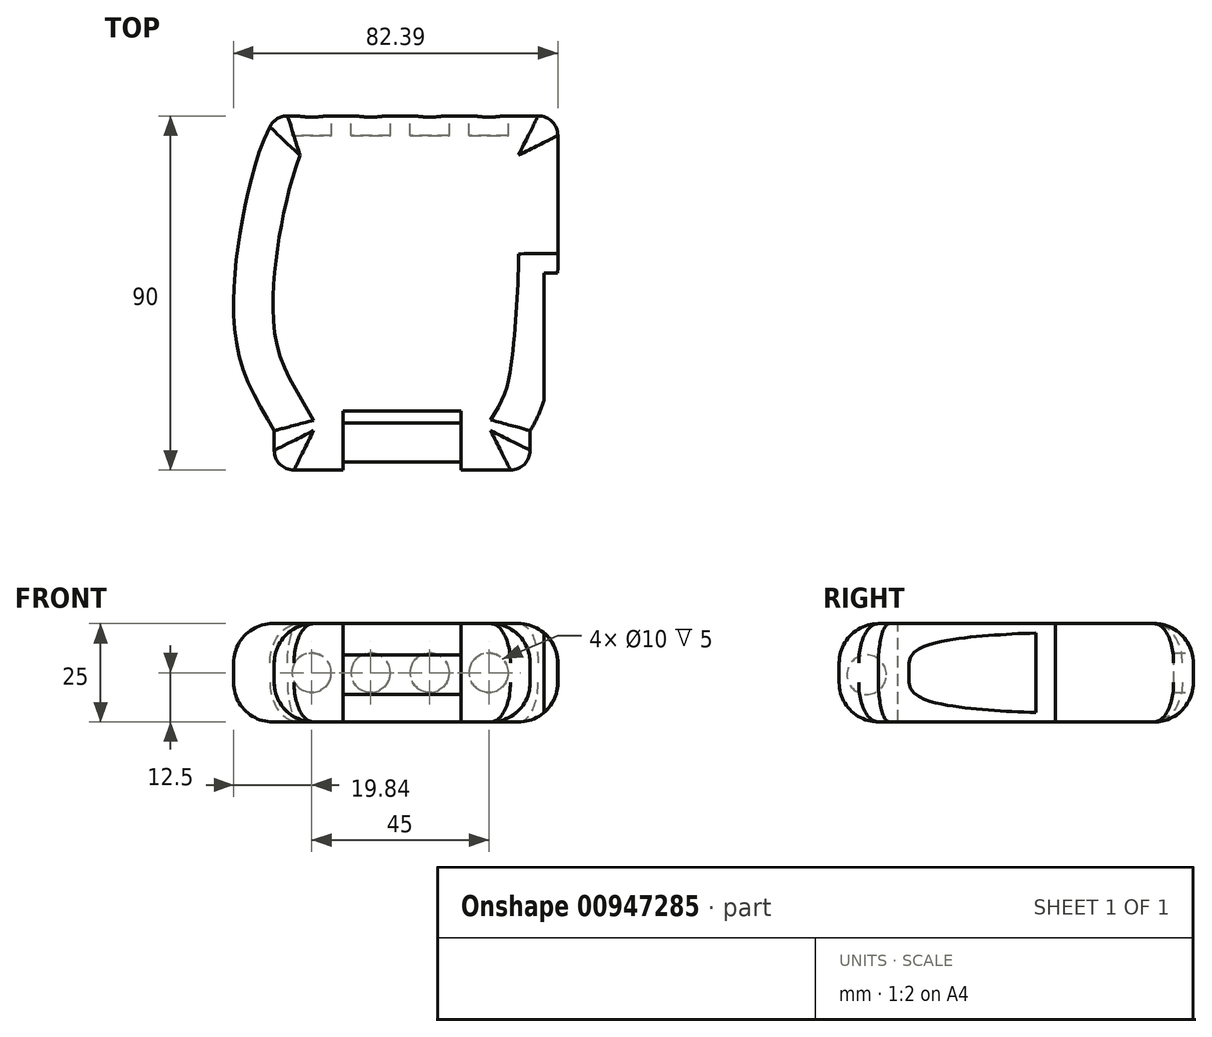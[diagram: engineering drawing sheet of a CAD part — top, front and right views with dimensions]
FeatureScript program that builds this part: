
annotation { "Feature Type Name" : "Feature", "Feature Type Description" : "" }
export const myFeature = defineFeature(function(context is Context, id is Id, definition is map)
    precondition{}
    {
        {
            var Q0;
            Q0=qCreatedBy(makeId("Top.planeOp"),FACE);
            var sketch = newSketch(context, id + "F0", { "sketchPlane" : qUnion([Q0])});
            skFitSpline(sketch, "E0", {"points": [v(-32.5, 0) * mm, v(-42.5, 25) * mm, v(-35.5, 73) * mm, v(-32.5, 80) * mm], "startDerivative": vector(-34.49, 60.35) * mm, "endDerivative": vector(0, 16.21) * mm});
            skFitSpline(sketch, "E1", {"points": [v(32.5, 0) * mm, v(37.5, 15) * mm, v(39.5, 40) * mm, v(39.5, 50) * mm], "startDerivative": vector(27.5, 45.82) * mm, "endDerivative": vector(0, 57.62) * mm});
            skLineSegment(sketch, "E2", {"start": v(-29.14, 80) * mm, "end": v(34.54, 80) * mm});
            skArc(sketch, "E3.filletArc", {"start": v(-29.14, 80) * mm, "mid": v(-31.78, 79.25) * mm, "end": v(-33.62, 77.2) * mm});
            skLineSegment(sketch, "E4", {"start": v(39.54, 75) * mm, "end": v(39.54, 45) * mm});
            skLineSegment(sketch, "E5.top", {"start": v(-27.5, -10) * mm, "end": v(27.5, -10) * mm});
            skLineSegment(sketch, "E5.left", {"start": v(-32.5, 0) * mm, "end": v(-32.5, -5) * mm});
            skLineSegment(sketch, "E5.right", {"start": v(32.5, 0) * mm, "end": v(32.5, -5) * mm});
            skArc(sketch, "E6.filletArc", {"start": v(39.54, 75) * mm, "mid": v(38.07, 78.54) * mm, "end": v(34.54, 80) * mm});
            skPoint(sketch, "E7.visualSharp", {"position": v(-32.5, -10) * mm});
            skArc(sketch, "E7.filletArc", {"start": v(-32.5, -5) * mm, "mid": v(-31.04, -8.54) * mm, "end": v(-27.5, -10) * mm});
            skPoint(sketch, "E8.visualSharp", {"position": v(32.5, -10) * mm});
            skArc(sketch, "E8.filletArc", {"start": v(27.5, -10) * mm, "mid": v(31.04, -8.54) * mm, "end": v(32.5, -5) * mm});
            skSolve(sketch);
        }
        {
            var Q0;
            Q0=makeQuery(id+"F0.imprint","IMPRINT",FACE,{"disambiguationData":[TD([[makeQuery(id+"F0.imprint","IMPRINT",EDGE,{"derivedFrom":sQuery(id+"F0.wireOp",EDGE,"E0")}),-1.0]])]});
            extrude(context, id + "F1", {"entities" : qUnion([Q0]), "depth" : 25 * mm, "offsetDistance" : 25 * mm});
        }
        {
            var Q0;
            Q0=makeQuery(id+"F1.opExtrude","CAP_FACE",FACE,{"disambiguationData":[OSD([sQuery(id+"F0.wireOp",EDGE,"49EKysyl-F1B6-WjAB-Oqjf-hUaWDvc0Rh3T"),sQuery(id+"F0.wireOp",EDGE,"E0"),sQuery(id+"F0.wireOp",EDGE,"E1"),sQuery(id+"F0.wireOp",EDGE,"E2"),sQuery(id+"F0.wireOp",EDGE,"E3.filletArc"),sQuery(id+"F0.wireOp",EDGE,"E4"),sQuery(id+"F0.wireOp",EDGE,"L64E4SzO-m6Dg-x3uf-Ctfk-5AHkUTRR6ZkJ"),sQuery(id+"F0.wireOp",EDGE,"5b3693cc-6a36-475d-aa05-17e4b2f90563.filletArc"),sQuery(id+"F0.wireOp",EDGE,"d782c81a-6095-4aa6-9554-ab9e2238e4e0.filletArc")])],"isStart":false});
            var Q1;
            Q1=makeQuery(id+"F1.opExtrude","CAP_FACE",FACE,{"disambiguationData":[OSD([sQuery(id+"F0.wireOp",EDGE,"49EKysyl-F1B6-WjAB-Oqjf-hUaWDvc0Rh3T"),sQuery(id+"F0.wireOp",EDGE,"E0"),sQuery(id+"F0.wireOp",EDGE,"E1"),sQuery(id+"F0.wireOp",EDGE,"E2"),sQuery(id+"F0.wireOp",EDGE,"E3.filletArc"),sQuery(id+"F0.wireOp",EDGE,"E4"),sQuery(id+"F0.wireOp",EDGE,"L64E4SzO-m6Dg-x3uf-Ctfk-5AHkUTRR6ZkJ"),sQuery(id+"F0.wireOp",EDGE,"5b3693cc-6a36-475d-aa05-17e4b2f90563.filletArc"),sQuery(id+"F0.wireOp",EDGE,"d782c81a-6095-4aa6-9554-ab9e2238e4e0.filletArc")])],"isStart":true});
            fillet(context, id + "F2", {"entities" : qUnion([Q0, Q1]), "tangentPropagation" : true, "radius" : 10 * mm, "defaultsChanged" : false, "vertexSettings" : [], "allowEdgeOverflow" : false});
        }
        {
            var Q0;
            Q0=makeQuery(id+"F1.opExtrude","CAP_FACE",FACE,{"disambiguationData":[OSD([sQuery(id+"F0.wireOp",EDGE,"E0"),sQuery(id+"F0.wireOp",EDGE,"E1"),sQuery(id+"F0.wireOp",EDGE,"E2"),sQuery(id+"F0.wireOp",EDGE,"E3.filletArc"),sQuery(id+"F0.wireOp",EDGE,"E4"),sQuery(id+"F0.wireOp",EDGE,"L64E4SzO-m6Dg-x3uf-Ctfk-5AHkUTRR6ZkJ"),sQuery(id+"F0.wireOp",EDGE,"5b3693cc-6a36-475d-aa05-17e4b2f90563.filletArc"),sQuery(id+"F0.wireOp",EDGE,"d782c81a-6095-4aa6-9554-ab9e2238e4e0.filletArc"),sQuery(id+"F0.wireOp",EDGE,"E5.top"),sQuery(id+"F0.wireOp",EDGE,"E5.left"),sQuery(id+"F0.wireOp",EDGE,"E5.right"),sQuery(id+"F0.wireOp",EDGE,"E6.filletArc"),sQuery(id+"F0.wireOp",EDGE,"E7.filletArc"),sQuery(id+"F0.wireOp",EDGE,"E8.filletArc")])],"isStart":false});
            var sketch = newSketch(context, id + "F3", { "sketchPlane" : qUnion([Q0])});
            skLineSegment(sketch, "E9.bottom", {"start": v(-15, 5) * mm, "end": v(15, 5) * mm});
            skLineSegment(sketch, "E9.top", {"start": v(-15, -10) * mm, "end": v(15, -10) * mm});
            skLineSegment(sketch, "E9.left", {"start": v(-15, 5) * mm, "end": v(-15, -10) * mm});
            skLineSegment(sketch, "E9.right", {"start": v(15, 5) * mm, "end": v(15, -10) * mm});
            skSolve(sketch);
        }
        {
            var Q0;
            Q0 = qSketchRegion(id + "F3", true);
            extrude(context, id + "F4", {"entities" : qUnion([Q0]), "operationType" : NewBodyOperationType.REMOVE, "oppositeDirection" : true, "depth" : 25 * mm, "offsetDistance" : 25 * mm});
        }
        {
            var Q0;
            Q0=makeQuery(id+"F4.boolean.opBoolean","COPY",FACE,{"derivedFrom":makeQuery(id+"F4.opExtrude","SWEPT_FACE",FACE,{"disambiguationData":[OSD([sQuery(id+"F3.wireOp",EDGE,"E9.left")])]})});
            var sketch = newSketch(context, id + "F5", { "sketchPlane" : qUnion([Q0])});
            skCircle(sketch, "E10", {"center": v(-3, 12) * mm, "radius": 5 * mm});
            skSolve(sketch);
        }
        {
            var Q0;
            Q0 = qSketchRegion(id + "F5", true);
            extrude(context, id + "F6", {"entities" : qUnion([Q0]), "operationType" : NewBodyOperationType.ADD, "depth" : 31 * mm, "offsetDistance" : 25 * mm});
        }
        {
            var Q0;
            Q0=makeQuery(id+"F1.opExtrude","SWEPT_FACE",FACE,{"disambiguationData":[OSD([sQuery(id+"F0.wireOp",EDGE,"E2")])]});
            var sketch = newSketch(context, id + "F7", { "sketchPlane" : qUnion([Q0])});
            skCircle(sketch, "E11", {"center": v(-22, 12.5) * mm, "radius": 5 * mm});
            skPoint(sketch, "E11.centerSnap0", {"position": v(-34.54, 12.5) * mm});
            skCircle(sketch, "E12.1.0.0", {"center": v(-7, 12.5) * mm, "radius": 5 * mm});
            skCircle(sketch, "E12.2.0.0", {"center": v(8, 12.5) * mm, "radius": 5 * mm});
            skCircle(sketch, "E12.3.0.0", {"center": v(23, 12.5) * mm, "radius": 5 * mm});
            skLineSegment(sketch, "E12.direction1", {"start": v(-20, 12.5) * mm, "end": v(-5, 12.5) * mm, "construction": true});
            skSolve(sketch);
        }
        {
            var Q0;
            Q0 = qSketchRegion(id + "F7", true);
            extrude(context, id + "F8", {"entities" : qUnion([Q0]), "operationType" : NewBodyOperationType.REMOVE, "oppositeDirection" : true, "depth" : 5 * mm, "offsetDistance" : 25 * mm});
        }
        {
            var Q0;
            Q0=makeQuery(id+"F1.opExtrude","CAP_FACE",FACE,{"disambiguationData":[OSD([sQuery(id+"F0.wireOp",EDGE,"E0"),sQuery(id+"F0.wireOp",EDGE,"E1"),sQuery(id+"F0.wireOp",EDGE,"E2"),sQuery(id+"F0.wireOp",EDGE,"E3.filletArc"),sQuery(id+"F0.wireOp",EDGE,"E4"),sQuery(id+"F0.wireOp",EDGE,"E5.top"),sQuery(id+"F0.wireOp",EDGE,"E5.left"),sQuery(id+"F0.wireOp",EDGE,"E5.right"),sQuery(id+"F0.wireOp",EDGE,"E6.filletArc"),sQuery(id+"F0.wireOp",EDGE,"E7.filletArc"),sQuery(id+"F0.wireOp",EDGE,"E8.filletArc")])],"isStart":false});
            var sketch = newSketch(context, id + "F9", { "sketchPlane" : qUnion([Q0])});
            skLineSegment(sketch, "E13.bottom", {"start": v(36, 40) * mm, "end": v(81, 40) * mm});
            skLineSegment(sketch, "E13.left", {"start": v(36, 40) * mm, "end": v(36, 7) * mm});
            skLineSegment(sketch, "E13.right", {"start": v(81, 40) * mm, "end": v(81, 7) * mm});
            skLineSegment(sketch, "E14", {"start": v(36, 7) * mm, "end": v(81, 7) * mm});
            skSolve(sketch);
        }
        {
            var Q0;
            Q0 = qSketchRegion(id + "F9", true);
            extrude(context, id + "F10", {"entities" : qUnion([Q0]), "operationType" : NewBodyOperationType.REMOVE, "oppositeDirection" : true, "depth" : 25 * mm, "offsetDistance" : 25 * mm});
        }
    });
